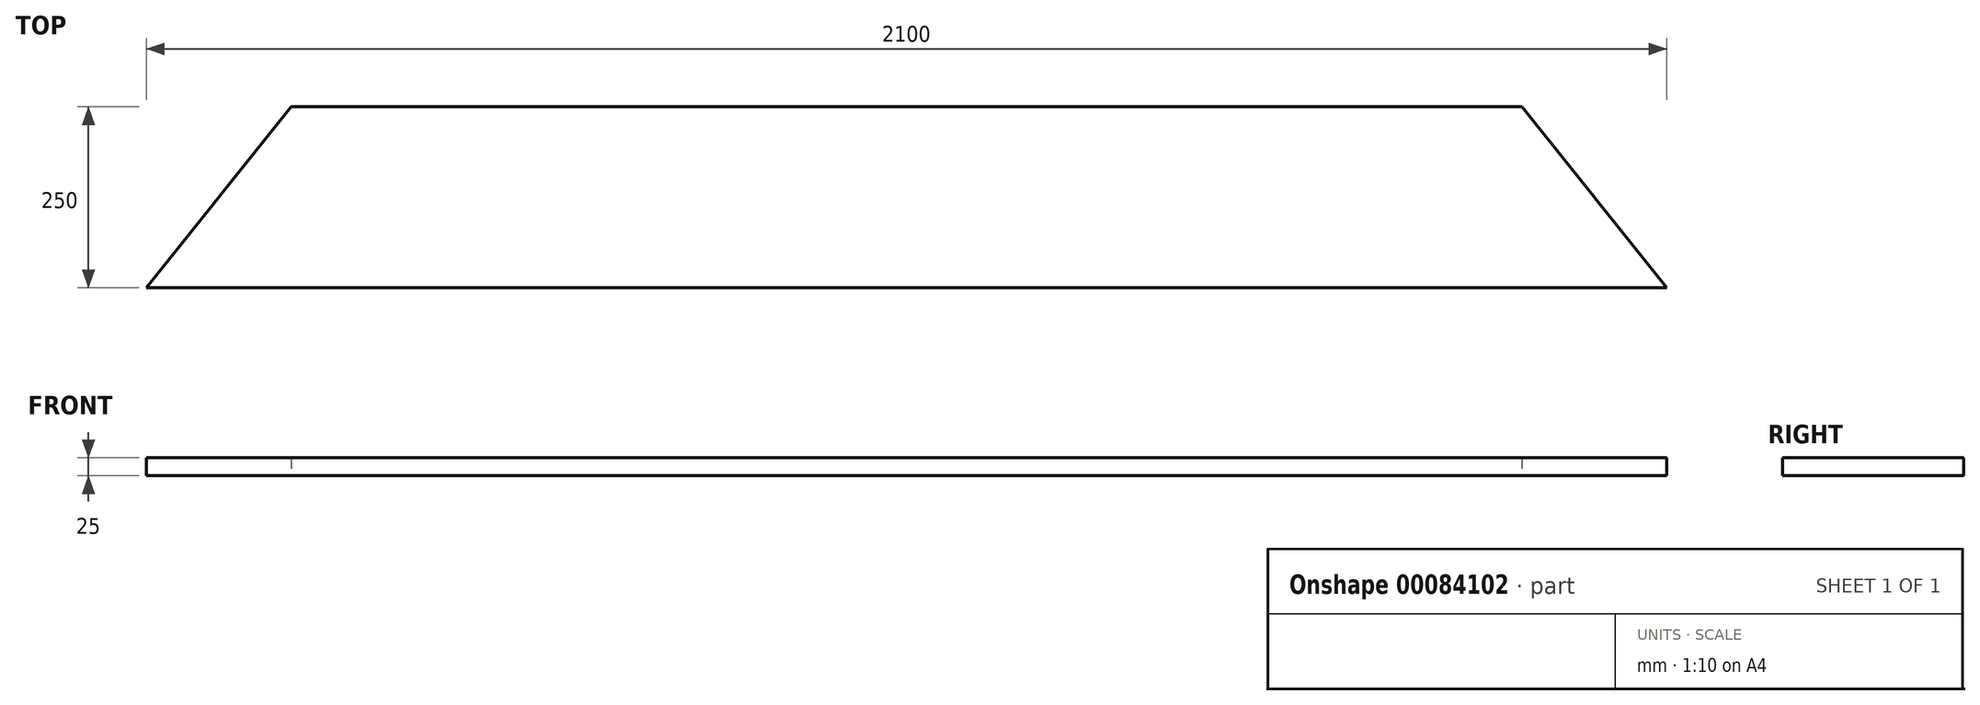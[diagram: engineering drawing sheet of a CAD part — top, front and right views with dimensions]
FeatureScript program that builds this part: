
annotation { "Feature Type Name" : "Feature", "Feature Type Description" : "" }
export const myFeature = defineFeature(function(context is Context, id is Id, definition is map)
    precondition{}
    {
        {
            var Q0;
            Q0=qCreatedBy(makeId("Top.planeOp"),FACE);
            var sketch = newSketch(context, id + "F0", { "sketchPlane" : qUnion([Q0])});
            skLineSegment(sketch, "E0.bottom", {"start": v(-817.65, 195.56) * mm, "end": v(882.35, 195.56) * mm});
            skLineSegment(sketch, "E0.top", {"start": v(-1017.65, -54.44) * mm, "end": v(1082.35, -54.44) * mm});
            skLineSegment(sketch, "E0.left", {"start": v(-817.65, 195.56) * mm, "end": v(-1017.65, -54.44) * mm});
            skLineSegment(sketch, "E0.right", {"start": v(1082.35, -54.44) * mm, "end": v(882.35, 195.56) * mm});
            skPoint(sketch, "E0.middle", {"position": v(32.35, -374.05) * mm});
            skPoint(sketch, "E1", {"position": v(32.35, -54.44) * mm});
            skPoint(sketch, "E2", {"position": v(32.35, 195.56) * mm});
            skSolve(sketch);
        }
        {
            var Q0;
            Q0=makeQuery(id+"F0.imprint","IMPRINT",FACE,{"disambiguationData":[TD([[makeQuery(id+"F0.imprint","IMPRINT",EDGE,{"derivedFrom":sQuery(id+"F0.wireOp",EDGE,"E0.bottom")}),-1.0]])]});
            extrude(context, id + "F1", {"entities" : qUnion([Q0]), "depth" : 25 * mm});
        }
    });
